# Revit family: QF_ELECTROLUXPROFESSIONAL_1LSNTM_WN6-14_E
name_source: partatom
category: Attrezzature speciali
units: mm (PartAtom-declared; Revit-internal decimal feet)

## family parameters
Basato su piano di lavoro = No
Condiviso = No
Punto di calcolo locali = No
Quota connettore circolare = Usa diametro
Sempre verticale = Sì
Taglio con vuoti quando caricato = No
Tipo di parte = Normale

## types (32) — shared parameters
Depth = 786.6 mm  [stored 2.58071 ft]
Depth Actual = 790 mm  [stored 2.59186 ft]
Height = 1218.8 mm  [stored 3.99869 ft]
Height Actual = 1220 mm  [stored 4.00262 ft]
Latent Heat Output = 0.0
Length Actual = 720 mm  [stored 2.3622 ft]
Modello = WN6-14
Produttore = Electrolux Professional
Sensible Heat Output = 0.0
URL = www.electroluxprofessional.com
Weight = 154
Width = 720 mm  [stored 2.3622 ft]
zero-valued in all types: Gas KW, Prospetto di default, Steam Pounds per Hour

## per-type parameters (varying)
| type | Cycle | Descrizione | Item Number | Phase | Volts | Watts |
| 9867730093 | 50 Hz | WASHER WN6-14 14KG EL 10KW 380-415/50/3N COMPASS PRO 6L01 ML 2xWATER POWDER+5xLIQ. VALV.CLOSED SILVER EXT.PM. 2.I/O DISC | 1LSP3N | 3 | 415 V | 10400 W |
| 9867730083 | 60 Hz | WASHER WN6-14 14KG NO HEAT 220-240/60/3 COMPASS PRO 6L01 ML 2xWATER POWDER VALV.OPEN SILVER DISCON. | 1LSP3K | 3 | 220 V | 800 W |
| 9867730250 | 60 Hz | WASHER WN6-14 14KG EL 10KW 220-240/60/3 COMPASS PRO 6G01 ML 2xWATER POWDER+5xLIQ. VALV.OPEN SST 2.I/O DISCON. STOP | 1LM0CA | 3 | 240 V | 8900 W |
| 9867730147 | 60 Hz | WASHER WN6-14 14KG NO HEAT 208-240/60/1 COMPASS PRO 6G01 ML 2xWATER POWDER+5xLIQ. VALV.CLOSED SILVER 2.I/O STOP | 1LSPD9 | 1 | 240 V | 800 W |
| 9867730127 | 50 Hz | WASHER WN6-14 14KG EL 10KW 380-415/50/3N COMPASS PRO 6H01 ML 2xWATER POWDER+5xLIQ. VALV.OPEN SST/SILVER 2.I/O DISCON. ST | 1LSP9L | 3 | 415 V | 10400 W |
| 9867730023 | 50 Hz | WASHER WN6-14 14KG NO HEAT 200/50/60/3 COMPASS PRO 6L41 JP,EN 2xWATER 5xLIQ. VALV.OPEN SILVER CM. JPY+KRW 2.I/O DISCON. | 1L822V | 3 | 200 V | 800 W |
| 9867730258 | 50 Hz | WASHER WN6-14 14KG EL 10KW 380-415/50/3 COMPASS PRO 6G07 ML 2xWATER POWDER+5xLIQ. VALV.OPEN SST 2.I/O TRAFO DISCON. STOP | 1LA26G | 3 | 415 V | 8800 W |
| 9867730076 | 50 Hz | WASHER WN6-14 14KG NO HEAT 220-240/50/1N COMPASS PRO 6L01 ML 2xWATER POWDER+5xLIQ. VALV.OPEN SILVER EXT.PM. 2.I/O DISCON | 1L823T | 1 | 240 V | 800 W |
| 9867730066 | 50 Hz | WASHER WN6-14 14KG EL 10KW 380-415/50/3 COMPASS PRO 6G01 ML 2xWATER POWDER VALV.OPEN SST/SILVER TRAFO DISCON. STOP | 1L824B | 3 | 415 V | 8800 W |
| 9867730238 | 50 Hz | WASHER WN6-14 14KG EL 10KW 380-415/50/3 COMPASS PRO 6G01 CH-EN 2xWATER POWDER VALV.OPEN SST/SILVER TRAFO DISCON. STOP | 1L0H5H | 3 | 415 V | 8800 W |
| 9867730243 | 60 Hz | WASHER WN6-14 14KG EL 10KW 220-240/60/3 COMPASS PRO 6G01 ML 2xWATER POWDER+5xLIQ. VALV.OPEN SILVER 2.I/O DISCON. STOP | 1L0H9Y | 3 | 240 V | 8800 W |
| 9867730256 | 60 Hz | WASHER WN6-14 14KG EL 10KW 380-415/60/3 COMPASS PRO 6G07 ML 2xWATER POWDER+5xLIQ. VALV.OPEN SILVER 2.I/O TRAFO DISCON. S | 1L82D4 | 3 | 415 V | 8800 W |
| 9867730246 | 50 Hz | WASHER WN6-14 14KG EL 7,5KW 380-415/50/3N COMPASS PRO 6A01 SE 2xWATER POWDER+5xLIQ. EL.VALV.OPEN SILVER 2.I/O DISCON. | 1L0HD2 | 3 | 415 V | 8000 W |
| 9867730065 | 50 Hz | WASHER WN6-14 14KG EL 10KW 380-415/50/3N COMPASS PRO 6G01 ML 2xWATER POWDER VALV.OPEN SILVER DISCON. STOP | 1L823R | 3 | 415 V | 8800 W |
| 9867730111 | 50 Hz | WASHER WN6-14 14KG NO HEAT 220-240/50/1N COMPASS PRO 6G01 ML 2xWATER POWDER+5xLIQ. VALV.OPEN SILVER 2.I/O DISCON. STOP | 1L0GC9 | 1 | 240 V | 800 W |
| 9867730131 | 60 Hz | WASHER WN6-14 14KG EL 10KW 480/60/3 COMPASS PRO 6G01 ML 2xWATER POWDER VALV.OPEN SST TRAFO DISCON. STOP | 1LSPAZ | 3 | 480 V | 10400 W |
| 9867730159 | 60 Hz | WASHER WN6-14 14KG EL 10KW 440/60/3 COMPASS PRO 6G01 ML 2xWATER POWDER+5xLIQ. VALV.OPEN SILVER 2.I/O QC TRAFO DISCON. ST | 1L0GLC | 3 | 440 V | 10500 W |
| 9867730251 | 60 Hz | WASHER WN6-14 14KG NO HEAT 220-240/60/3 COMPASS PRO 6G01 CH-EN 2xWATER POWDER VALV.OPEN SILVER DISCON. STOP | 1L82CU | 3 | 220 V | 800 W |
| 9867730146 | 60 Hz | WASHER WN6-14 14KG EL 10KW 380-415/60/3N COMPASS PRO 6G01 ML 2xWATER POWDER+5xLIQ. VALV.CLOSED SILVER 2.I/O DISCON. STOP | 1LSPD8 | 3 | 415 V | 10400 W |
| 9867730106 | 50 Hz | WASHER WN6-14 14KG EL 10KW 380-415/220-240/50/3N/1 COMPASS PRO 6G01 ML 2xWATER POWDER+5xLIQ. VALV.OPEN SILVER 2.I/O DISC | 1L0GBH | 3 | 415 V | 10400 W |
| 9867730231 | 60 Hz | WASHER WN6-14 14KG EL 10KW 220-240/60/3 COMPASS PRO 6G01 ML 2xWATER POWDER VALV.OPEN SST/SILVER DISCON. STOP | 1L0H3B | 3 | 240 V | 8800 W |
| 9867730136 | 50 Hz | WASHER WN6-14 14KG NO HEAT 220-240/50/1N COMPASS PRO 6G01 ML 2xWATER POWDER+5xLIQ. VALV.CLOSED SILVER 2.I/O DISCON. STOP | 1L0GF6 | 1 | 240 V | 800 W |
| 9867730077 | 50 Hz | WASHER WN6-14 14KG EL 10KW 380-415/220-240/50/3N/3 COMPASS PRO 6G01 ML 2xWATER POWDER+5xLIQ. VALV.OPEN SILVER 2.I/O DISC | 1L823U | 3 | 415 V | 10400 W |
| 9867730229 | 50 Hz | WASHER WN6-14 14KG EL 10KW 380-415/50/3 COMPASS PRO 6G07 ML 2xWATER POWDER+5xLIQ. VALV.OPEN SILVER 2.I/O TRAFO DISCON. S | 1LSRJ9 | 3 | 415 V | 8800 W |
| 9867730143 | 60 Hz | WASHER WN6-14 14KG EL 10KW 220-230/60/1 COMPASS PRO 6G07 ML 2xWATER POWDER+5xLIQ. VALV.OPEN SST 2.I/O QC DISCON. STOP | 1LA1E2 | 1 | 240 V | 10400 W |
| 9867730092 | 60 Hz | WASHER WN6-14 14KG EL 10KW 440/60/3 COMPASS PRO 6G01 ML 2xWATER POWDER VALV.OPEN SST/SILVER TRAFO DISCON. STOP | 1L8241 | 3 | 440 V | 10500 W |
| 9867730123 | 50 Hz | WASHER WN6-14 14KG NO HEAT 220-240/50/1N COMPASS PRO 6G01 ML 2xWATER POWDER VALV.OPEN SILVER DISCON. STOP | 1LA1CS | 1 | 240 V | 800 W |
| 9867730257 | 50 Hz | WASHER WN6-14 14KG EL 10KW 380-415/50/3N COMPASS PRO 6G01 ML 2xWATER POWDER+5xLIQ. VALV.CLOSED SILVER 2.I/O DISCON. STOP | 1LA26F | 3 | 415 V | 8800 W |
| 9867730195 | 60 Hz | WASHER WN6-14 14KG EL 10KW 220-240/60/1 COMPASS PRO 6G07 ML 2xWATER POWDER+5xLIQ. VALV.OPEN SST/SILVER 2.I/O QC DISCON. | 1L0GXL | 1 | 240 V | 10400 W |
| 9867730178 | 50 Hz | WASHER WN6-14 14KG EL 10KW 380-415/220-240/50/3N/3 COMPASS PRO 6B01 ML 2xWATER POWDER+5xLIQ. VALV.OPEN SILVER 2.I/O DISC | 1L0GU3 | 3 | 415 V | 10400 W |
| 9867730135 | 50 Hz | WASHER WN6-14 14KG EL 10KW 380-415/220-240/50/3N/3 COMPASS PRO 6G01 ML 2xWATER POWDER+5xLIQ. VALV.CLOSED SILVER 2.I/O DI | 1L0GF5 | 3 | 415 V | 10400 W |
| 9867730255 | 50 Hz | WASHER WN6-14 14KG EL 10KW 220-240/50/1 COMPASS PRO 6G07 ML 2xWATER POWDER+5xLIQ. VALV.OPEN SST/SILVER 2.I/O QC DISCON. | 1L82D0 | 1 | 240 V | 8900 W |

note: [stored X ft] marks values corroborated as IEEE doubles in the binary element streams (Revit-internal decimal feet)

## geometry (parser evidence)
native form markers: Sweep x5
no freeform markers — native parametric forms only
